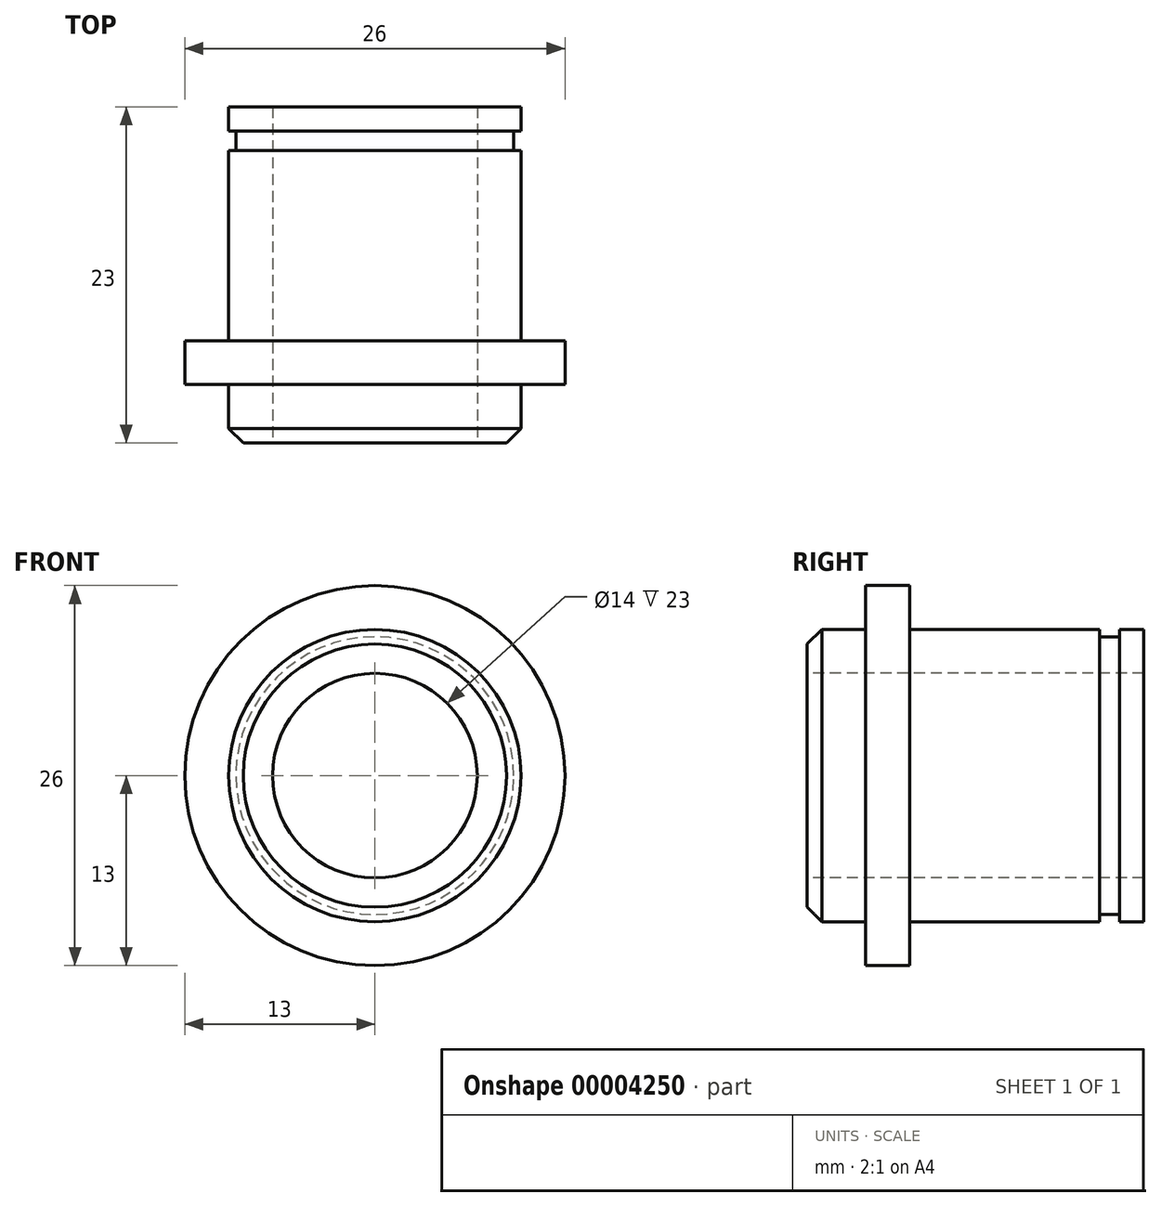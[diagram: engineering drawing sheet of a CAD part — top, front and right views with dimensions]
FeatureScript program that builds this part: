
annotation { "Feature Type Name" : "Feature", "Feature Type Description" : "" }
export const myFeature = defineFeature(function(context is Context, id is Id, definition is map)
    precondition{}
    {
        {
            var Q0;
            Q0=qCreatedBy(makeId("Right.planeOp"),FACE);
            var sketch = newSketch(context, id + "F0", { "sketchPlane" : qUnion([Q0])});
            skLineSegment(sketch, "E0", {"start": v(0, 7) * mm, "end": v(0, 10) * mm});
            skLineSegment(sketch, "E1", {"start": v(0, 10) * mm, "end": v(4, 10) * mm});
            skLineSegment(sketch, "E2", {"start": v(4, 10) * mm, "end": v(4, 13) * mm});
            skLineSegment(sketch, "E3", {"start": v(4, 13) * mm, "end": v(7, 13) * mm});
            skLineSegment(sketch, "E4", {"start": v(7, 13) * mm, "end": v(7, 10) * mm});
            skLineSegment(sketch, "E5", {"start": v(7, 10) * mm, "end": v(20, 10) * mm});
            skLineSegment(sketch, "E6", {"start": v(20, 10) * mm, "end": v(20, 9.5) * mm});
            skLineSegment(sketch, "E7", {"start": v(20, 9.5) * mm, "end": v(21.35, 9.5) * mm});
            skLineSegment(sketch, "E8", {"start": v(21.35, 9.5) * mm, "end": v(21.35, 10) * mm});
            skLineSegment(sketch, "E9", {"start": v(21.35, 10) * mm, "end": v(23, 10) * mm});
            skLineSegment(sketch, "E10", {"start": v(23, 10) * mm, "end": v(23, 7) * mm});
            skLineSegment(sketch, "E11", {"start": v(23, 7) * mm, "end": v(0, 7) * mm});
            skLineSegment(sketch, "E12", {"start": v(0, 0) * mm, "end": v(50.14, 0) * mm, "construction": true});
            skSolve(sketch);
        }
        {
            var Q0;
            Q0=makeQuery(id+"F0.imprint","IMPRINT",FACE,{"disambiguationData":[TD([[makeQuery(id+"F0.imprint","IMPRINT",EDGE,{"derivedFrom":sQuery(id+"F0.wireOp",EDGE,"E0")}),-1.0]])]});
            var Q1;
            Q1=sQuery(id+"F0.wireOp",EDGE,"E12");
            revolve(context, id + "F1", {"entities" : qUnion([Q0]), "axis" : qUnion([Q1]), "revolveType" : RevolveType.FULL});
        }
        {
            var Q0;
            Q0=makeQuery(id+"F1.opRevolve","SWEPT_EDGE",EDGE,{"disambiguationData":[OSD([sQuery(id+"F0.wireOp",EDGE,"E0"),sQuery(id+"F0.wireOp",EDGE,"E1")])]});
            chamfer(context, id + "F2", {"entities" : qUnion([Q0]), "width" : 1 * mm, "tangentPropagation" : true});
        }
    });
